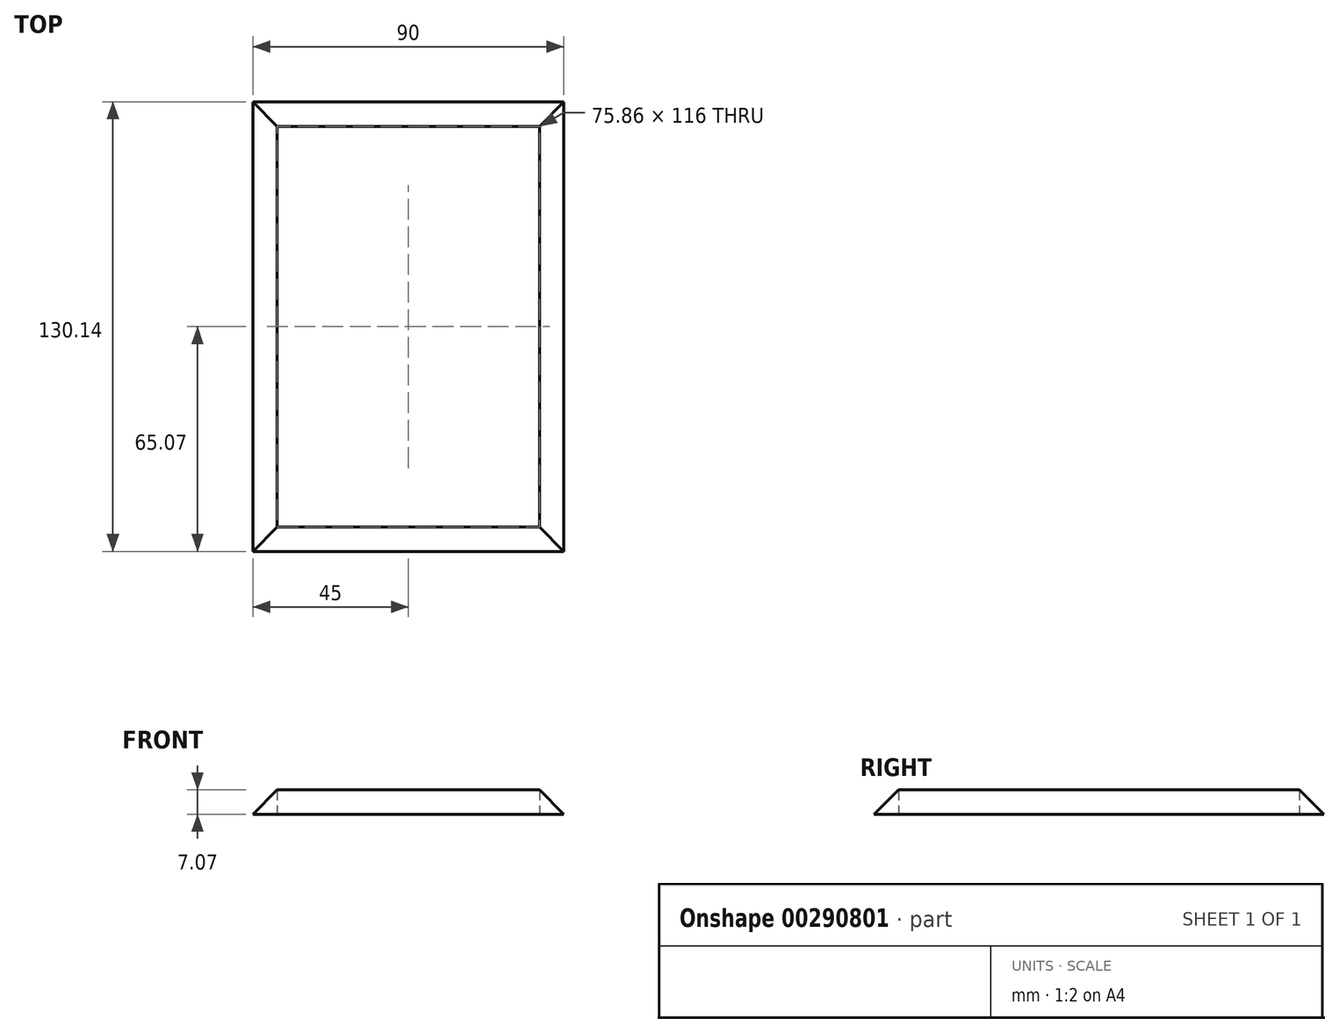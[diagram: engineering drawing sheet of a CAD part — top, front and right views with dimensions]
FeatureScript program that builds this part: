
annotation { "Feature Type Name" : "Feature", "Feature Type Description" : "" }
export const myFeature = defineFeature(function(context is Context, id is Id, definition is map)
    precondition{}
    {
        {
            var Q0;
            Q0=qCreatedBy(makeId("Top.planeOp"),FACE);
            var sketch = newSketch(context, id + "F0", { "sketchPlane" : qUnion([Q0])});
            skLineSegment(sketch, "E0.bottom", {"start": v(-45, 65.07) * mm, "end": v(45, 65.07) * mm});
            skLineSegment(sketch, "E0.top", {"start": v(-45, -65.07) * mm, "end": v(45, -65.07) * mm});
            skLineSegment(sketch, "E0.left", {"start": v(-45, 65.07) * mm, "end": v(-45, -65.07) * mm});
            skLineSegment(sketch, "E0.right", {"start": v(45, 65.07) * mm, "end": v(45, -65.07) * mm});
            skPoint(sketch, "E0.middle", {"position": v(0, 0) * mm});
            skLineSegment(sketch, "E1.0", {"start": v(-37.93, -58) * mm, "end": v(37.93, -58) * mm});
            skLineSegment(sketch, "E1.1", {"start": v(-37.93, 58) * mm, "end": v(-37.93, -58) * mm});
            skLineSegment(sketch, "E1.2", {"start": v(-37.93, 58) * mm, "end": v(37.93, 58) * mm});
            skLineSegment(sketch, "E1.3", {"start": v(37.93, 58) * mm, "end": v(37.93, -58) * mm});
            skSolve(sketch);
        }
        {
            var Q0;
            Q0=makeQuery(id+"F0.imprint","IMPRINT",FACE,{"disambiguationData":[TD([[makeQuery(id+"F0.imprint","IMPRINT",EDGE,{"derivedFrom":sQuery(id+"F0.wireOp",EDGE,"E0.bottom")}),-1.0]])]});
            extrude(context, id + "F1", {"entities" : qUnion([Q0]), "depth" : 7.07 * mm});
        }
        {
            var Q0;
            Q0=makeQuery(id+"F1.opExtrude","CAP_EDGE",EDGE,{"disambiguationData":[OSD([sQuery(id+"F0.wireOp",EDGE,"E0.left")])],"isStart":false});
            var Q1;
            Q1=makeQuery(id+"F1.opExtrude","CAP_EDGE",EDGE,{"disambiguationData":[OSD([sQuery(id+"F0.wireOp",EDGE,"E0.bottom")])],"isStart":false});
            var Q2;
            Q2=makeQuery(id+"F1.opExtrude","CAP_EDGE",EDGE,{"disambiguationData":[OSD([sQuery(id+"F0.wireOp",EDGE,"E0.right")])],"isStart":false});
            var Q3;
            Q3=makeQuery(id+"F1.opExtrude","CAP_EDGE",EDGE,{"disambiguationData":[OSD([sQuery(id+"F0.wireOp",EDGE,"E0.top")])],"isStart":false});
            chamfer(context, id + "F2", {"entities" : qUnion([Q0, Q1, Q2, Q3]), "width" : 7.07 * mm, "tangentPropagation" : true});
        }
    });
